# Revit family: 1 SOUND_Cannon Series Freestanding
name_source: partatom
category: Communication Devices
units: mm (PartAtom-declared; Revit-internal decimal feet)

## family parameters
Always vertical = No
Cut with Voids When Loaded = No
Maintain Annotation Orientation = No
Part Type = Normal
Room Calculation Point = No
Round Connector Dimension = Use Diameter
Shared = No
Work Plane-Based = Yes

## types (5) — shared parameters
Category = Speaker
Construction = Finland birch plywood (phenolic glue), polyurea, clear matte salt and UV resistant coating, 316 stainless steel hardware, 3D spacer mesh fabric
Default Elevation = 2438 mm
Manufacturer = 1 SOUND
Rigging = (4) M6 points
URL = https://www.1-sound.com

## per-type parameters (varying)
| type | Bandwidth | Connectors | Dimensions (HxWxD) | Impedance | Power | Speaker Model | Weight |
| C4i | 100 Hz - 18 kHz (-6 dB) | (1) screw terminal block with input +/- and loop +/- | 5.9” (150 mm) x 5.9” (150 mm) x 7” (180 mm) | 8Ω | 200 watts (continuous), 100 watts (AES) | 1 SOUND_Cannon_C4i : C4i | 5.1 lb / 2.3 kg |
| C5i | 65 Hz - 18 kHz (-6 dB) | (1) screw terminal block with input +/- and loop +/- | 7.5” (190 mm) x 7.5” (190 mm) x 8.2” (208 mm) | 16Ω | 240 watts (continuous), 120 watts (AES) | 1 SOUND_Cannon_C5 : C5i | 9.4 lb / 4.3 kg |
| C5 | 65 Hz - 18 kHz (-6 dB) | (2) NL4, 2-circuit switch | 7.5” (190 mm) x 7.5” (190 mm) x 8.2” (208 mm) | 16Ω | 240 watts (continuous), 120 watts (AES) | 1 SOUND_Cannon_C5 : C5 | 9.4 lb / 4.3 kg |
| C6i | 60 Hz - 18 kHz (-6 dB) | (1) screw terminal block with input +/- and loop +/- | 8.5” (216 mm) x 8.5” (216 mm) x 8.2” (208 mm) | 16Ω | 240 watts (continuous), 120 watts (AES) | 1 SOUND_Cannon_C6 : C6i | 10.6 lb / 4.8 kg |
| C6 | 60 Hz - 18 kHz (-6 dB) | (2) NL4, 2-circuit switch | 8.5” (216 mm) x 8.5” (216 mm) x 8.2” (208 mm) | 16Ω | 240 watts (continuous), 120 watts (AES) | 1 SOUND_Cannon_C6 : C6 | 10.6 lb / 4.8 kg |

note: column(s) folded — value = type name in every type: Model

## geometry (parser evidence)
native form markers: Sweep x33
no freeform markers — native parametric forms only
